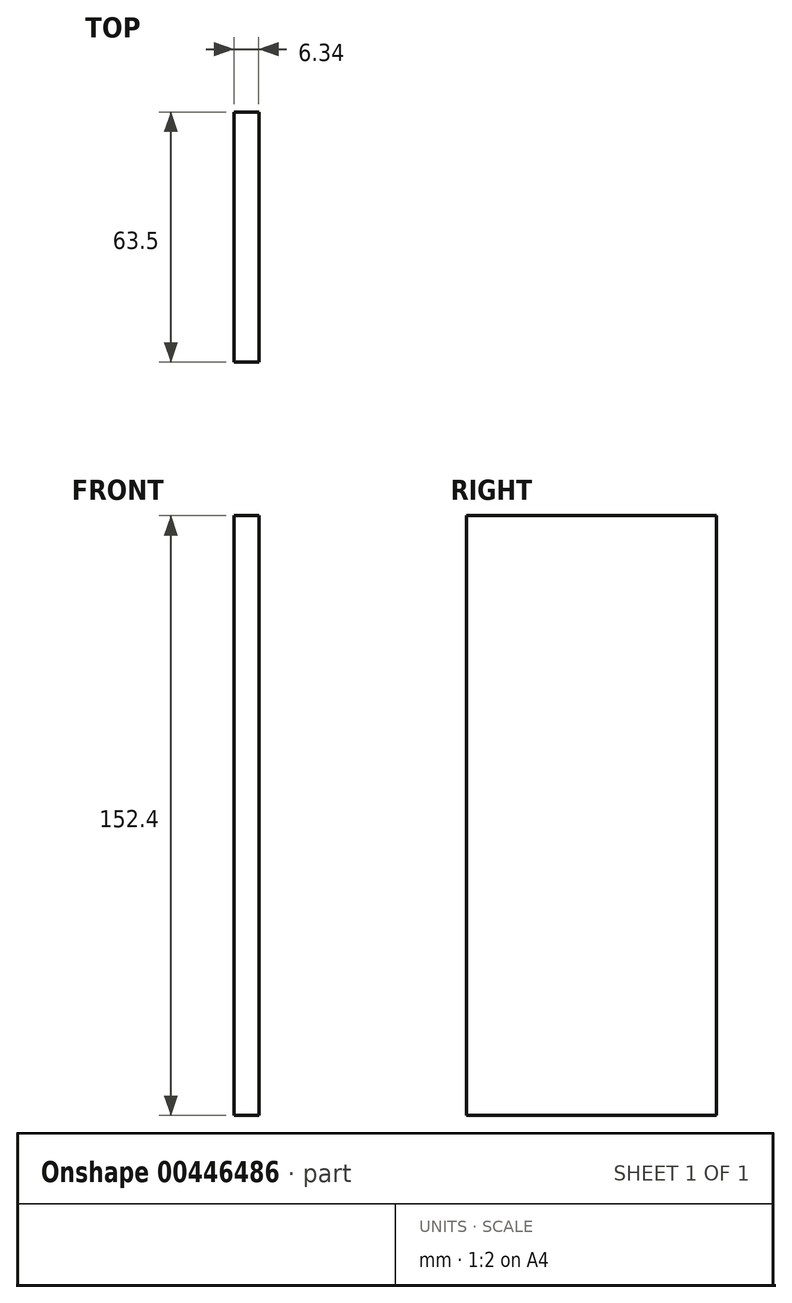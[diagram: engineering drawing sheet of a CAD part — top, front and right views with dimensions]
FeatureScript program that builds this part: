
annotation { "Feature Type Name" : "Feature", "Feature Type Description" : "" }
export const myFeature = defineFeature(function(context is Context, id is Id, definition is map)
    precondition{}
    {
        {
            var Q0;
            Q0=qCreatedBy(makeId("Front.planeOp"),FACE);
            var sketch = newSketch(context, id + "F0", { "sketchPlane" : qUnion([Q0])});
            skLineSegment(sketch, "E0.bottom", {"start": v(3.17, 76.2) * mm, "end": v(-3.18, 76.2) * mm});
            skLineSegment(sketch, "E0.top", {"start": v(3.18, -76.2) * mm, "end": v(-3.17, -76.2) * mm});
            skLineSegment(sketch, "E0.left", {"start": v(3.17, 76.2) * mm, "end": v(3.18, -76.2) * mm});
            skLineSegment(sketch, "E0.right", {"start": v(-3.18, 76.2) * mm, "end": v(-3.17, -76.2) * mm});
            skPoint(sketch, "E0.middle", {"position": v(0, 0) * mm});
            skPoint(sketch, "E1", {"position": v(0, -76.2) * mm});
            skSolve(sketch);
        }
        {
            var Q0;
            Q0=makeQuery(id+"F0.imprint","IMPRINT",FACE,{"disambiguationData":[TD([[makeQuery(id+"F0.imprint","IMPRINT",EDGE,{"derivedFrom":sQuery(id+"F0.wireOp",EDGE,"E0.bottom")}),1.0]])]});
            extrude(context, id + "F1", {"entities" : qUnion([Q0]), "depth" : 63.5 * mm, "symmetric" : true});
        }
    });
